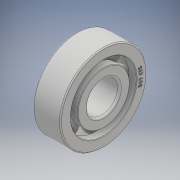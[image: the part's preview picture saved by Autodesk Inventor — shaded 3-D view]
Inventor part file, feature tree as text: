
AUTODESK INVENTOR PART (.ipt)
format: ipt  version: 2018 (Build 220112000, 112)  size: 660,480 bytes
history: native  units: mm
features: other x8, revolve x2
ambient origin geometry x8: Origin, YZ Plane, XZ Plane, XY Plane, X Axis, Y Axis, Z Axis, Center Point
bodies: Solid1 (feature_tree), Solid2 (feature_tree), Solid3 (feature_tree), Solid4 (feature_tree), Solid5 (feature_tree), Solid6 (feature_tree), Solid7 (feature_tree), Solid8 (feature_tree), Solid9 (feature_tree), Solid10 (feature_tree)
feature tree (10):
  revolve  "Revolve1[1]"  [1 undecoded]
  other  "Wrap1"
  revolve  "Revolve2"  [1 undecoded]
  other  "CirPattern1[1]"
  other  "CirPattern1[2]"
  other  "CirPattern1[3]"
  other  "CirPattern1[4]"
  other  "CirPattern1[5]"
  other  "CirPattern1[6]"
  other  "CirPattern1[7]"
note: 2 required parameter values undecoded (feature->parameter linkage not recoverable at this tier; creation-order binding heuristic only, values carry confidence <= 0.55)
